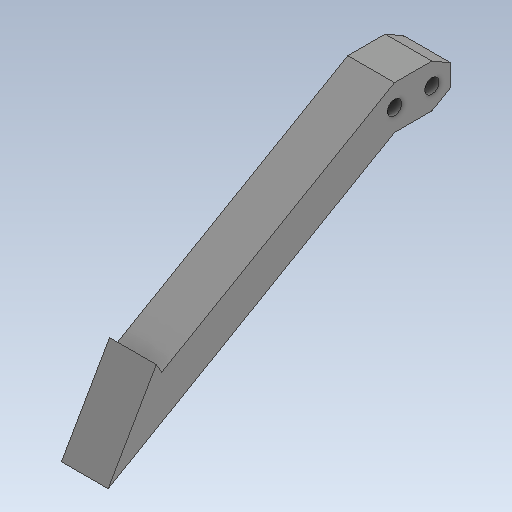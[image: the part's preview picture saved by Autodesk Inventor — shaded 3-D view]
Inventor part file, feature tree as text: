
AUTODESK INVENTOR PART (.ipt)
format: ipt  version: 2020 (Build 240168000, 168)  size: 154,112 bytes
history: native  units: in
note: dims shown in document units (in); Inventor stores cm internally (conversion verified against a paired STEP export)
features: extrude x1, sketch x1
ambient origin geometry x8: Origin, YZ Plane, XZ Plane, XY Plane, X Axis, Y Axis, Z Axis, Center Point
bodies: Body1 (feature_tree)
feature tree (2):
  extrude  "Extrusion2"  Depth=0.3937in
  sketch  "Sketch1"  dims[d3=0.1818in d4=0.6299in d15=0.315in d16=0.315in d18=0.122in d19=0.122in d20=0.1818in d23=0.0787in d24=1.5752in d25=60.0deg d26=30.0deg d27=2.8858in d32=0.3937in d33=0.0in]
